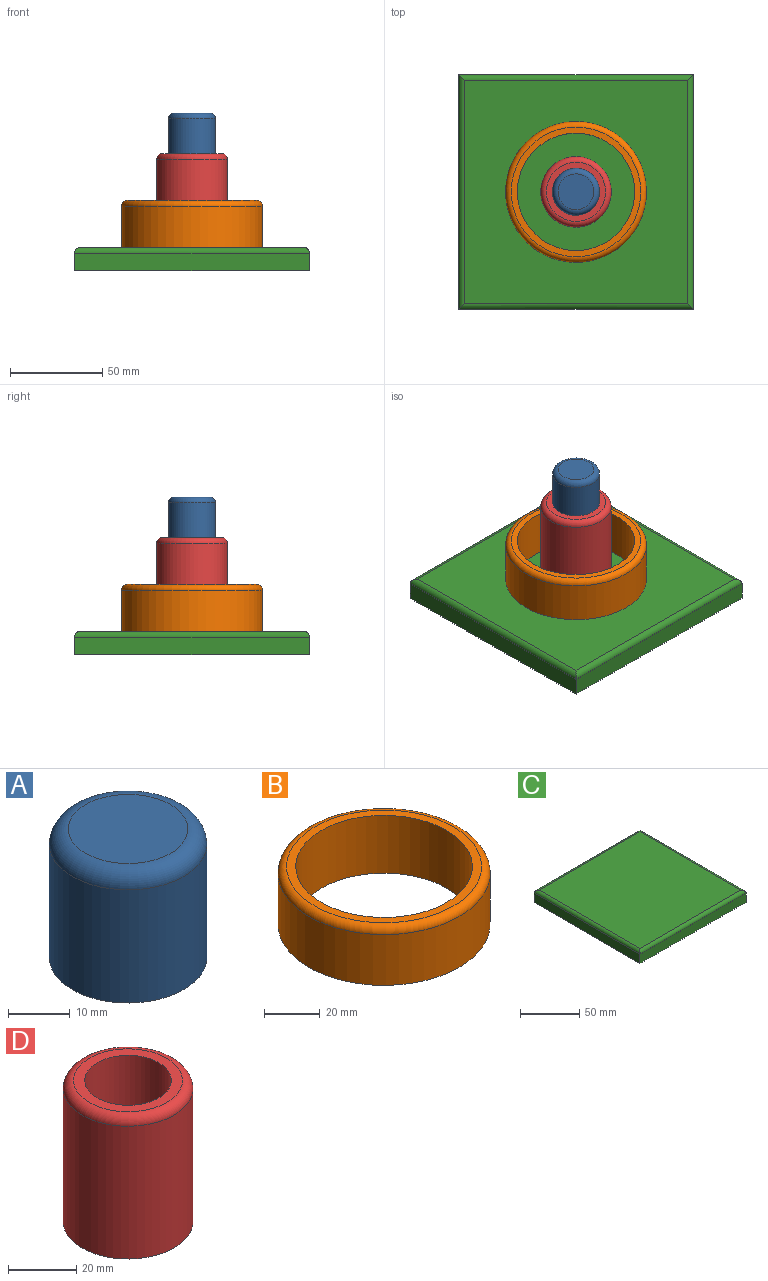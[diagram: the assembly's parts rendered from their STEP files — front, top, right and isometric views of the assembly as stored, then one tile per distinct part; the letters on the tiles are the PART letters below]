
ASSEMBLY  parts=4 mates=3
PART A: 4 faces, bbox 27.5x27.5x25.4 mm
  f0: cylinder r=12.7mm len=25.4mm, axis (0,0,-1), area 1783.6mm2, adj f2,f3
  f1: plane 19.3x19.3mm, normal (0,0,1), area 292.7mm2, adj f3
  f2: plane 25.4x25.4mm, normal (0,0,-1), area 506.7mm2, adj f0
  f3: torus R=9.65mm, axis (0,0,1), area 348.7mm2, adj f0,f1
PART B: 5 faces, bbox 82.5x82.5x25.4 mm
  f0: cylinder r=31.75mm len=63.5mm, axis (0,0,-1), area 5067.1mm2, adj f2,f3
  f1: cylinder r=38.1mm len=76.2mm, axis (0,0,-1), area 5350.8mm2, adj f3,f4
  f2: plane 70.1x70.1mm, normal (0,0,1), area 693mm2, adj f0,f4
  f3: plane 76.2x76.2mm, normal (0,0,-1), area 1393.4mm2, adj f0,f1
  f4: torus R=35.05mm, axis (0,0,1), area 1112.8mm2, adj f1,f2
PART C: 10 faces, bbox 127x127x12.7 mm
  f0: plane 127x9.65mm, normal (0,1,0), area 1225.8mm2, adj f1,f3,f5,f6
  f1: plane 127x9.65mm, normal (-1,0,0), area 1225.8mm2, adj f0,f2,f5,f7
  f2: plane 127x9.65mm, normal (0,-1,0), area 1225.8mm2, adj f1,f3,f5,f9
  f3: plane 127x9.65mm, normal (1,0,0), area 1225.8mm2, adj f0,f2,f5,f8
  f4: plane 120.9x120.9mm, normal (0,0,1), area 14617.8mm2, adj f6,f7,f8,f9
  f5: plane 127x127mm, normal (0,0,-1), area 16129mm2, adj f0,f1,f2,f3
  f6: cylinder r=3.05mm len=127mm, axis (1,0,0), area 597.4mm2, adj f0,f4,f7,f8
  f7: cylinder r=3.05mm len=127mm, axis (0,1,0), area 597.4mm2, adj f1,f4,f6,f9
  f8: cylinder r=3.05mm len=127mm, axis (0,-1,0), area 597.4mm2, adj f3,f4,f6,f9
  f9: cylinder r=3.05mm len=127mm, axis (-1,0,0), area 597.4mm2, adj f2,f4,f7,f8
PART D: 5 faces, bbox 41.2x41.2x50.8 mm
  f0: cylinder r=12.7mm len=50.8mm, axis (0,0,-1), area 4053.7mm2, adj f2,f3
  f1: cylinder r=19.05mm len=47.75mm, axis (0,0,-1), area 5715.7mm2, adj f3,f4
  f2: plane 32x32mm, normal (0,0,1), area 297.7mm2, adj f0,f4
  f3: plane 38.1x38.1mm, normal (0,0,-1), area 633.4mm2, adj f0,f1
  f4: torus R=16mm, axis (0,0,1), area 539.8mm2, adj f1,f2
PLACE A rot(axis=(0,0,1),1.2deg) t=(0.47,-0.27,-3.23)mm
PLACE B rot(axis=(0,0,-1),175.3deg) t=(0.47,-0.27,0.3)mm
PLACE C t=(0.47,-0.27,0.3)mm fixed
PLACE D t=(0.47,-0.27,0.3)mm
MATE cylindrical B.f0 <-> D.f0  axis (0,0,1) through (0.47,-0.27,38.4)mm
MATE cylindrical A.f0 <-> D.f0  axis (0,0,-1) through (0.47,-0.27,60.27)mm
MATE fastened C.f4 <-> D.f0  axis (0,0,1) through (0.47,-0.27,13)mm
